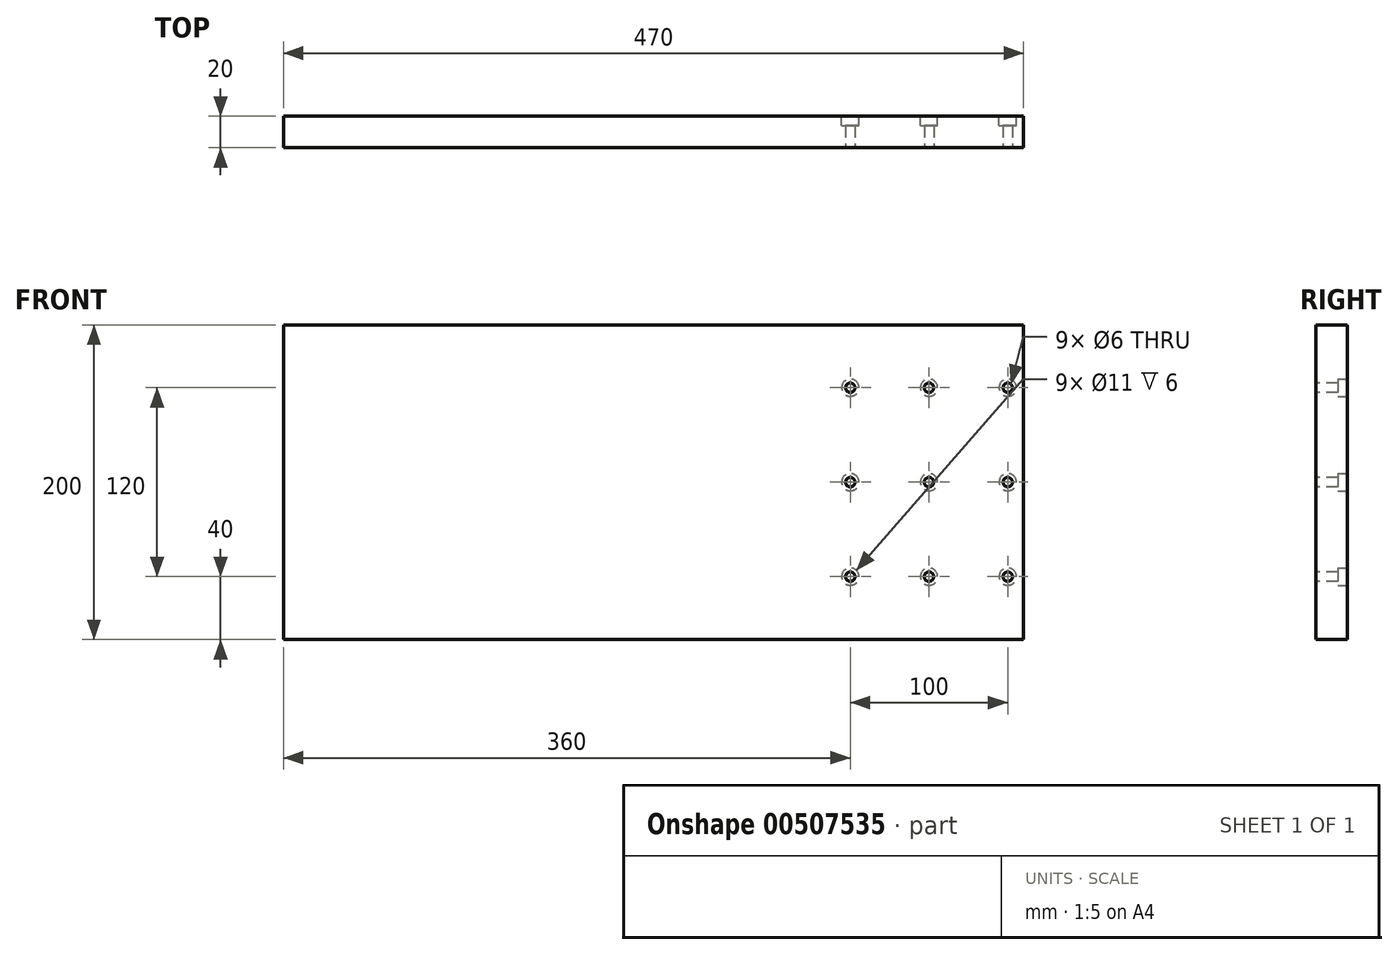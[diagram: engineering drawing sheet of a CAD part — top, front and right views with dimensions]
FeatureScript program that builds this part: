
annotation { "Feature Type Name" : "Feature", "Feature Type Description" : "" }
export const myFeature = defineFeature(function(context is Context, id is Id, definition is map)
    precondition{}
    {
        {
            var Q0;
            Q0=qCreatedBy(makeId("Front.planeOp"),FACE);
            var sketch = newSketch(context, id + "F0", { "sketchPlane" : qUnion([Q0])});
            skLineSegment(sketch, "E0.bottom", {"start": v(0, 0) * mm, "end": v(470, 0) * mm});
            skLineSegment(sketch, "E0.top", {"start": v(0, 200) * mm, "end": v(470, 200) * mm});
            skLineSegment(sketch, "E0.left", {"start": v(0, 0) * mm, "end": v(0, 200) * mm});
            skLineSegment(sketch, "E0.right", {"start": v(470, 0) * mm, "end": v(470, 200) * mm});
            skSolve(sketch);
        }
        {
            var Q0;
            Q0=makeQuery(id+"F0.imprint","IMPRINT",FACE,{"disambiguationData":[TD([[makeQuery(id+"F0.imprint","IMPRINT",EDGE,{"derivedFrom":sQuery(id+"F0.wireOp",EDGE,"E0.bottom")}),1.0]])]});
            extrude(context, id + "F1", {"entities" : qUnion([Q0]), "depth" : 20 * mm});
        }
        {
            var Q0;
            Q0=makeQuery(id+"F1.opExtrude","CAP_FACE",FACE,{"disambiguationData":[OSD([sQuery(id+"F0.wireOp",EDGE,"E0.bottom"),sQuery(id+"F0.wireOp",EDGE,"E0.top"),sQuery(id+"F0.wireOp",EDGE,"E0.left"),sQuery(id+"F0.wireOp",EDGE,"E0.right")])],"isStart":false});
            var sketch = newSketch(context, id + "F2", { "sketchPlane" : qUnion([Q0])});
            skCircle(sketch, "E1", {"center": v(360, 160) * mm, "radius": 3 * mm});
            skCircle(sketch, "E2", {"center": v(360, 100) * mm, "radius": 3 * mm});
            skCircle(sketch, "E3", {"center": v(360, 40) * mm, "radius": 3 * mm});
            skCircle(sketch, "E4", {"center": v(410, 160) * mm, "radius": 3 * mm});
            skCircle(sketch, "E5", {"center": v(410, 100) * mm, "radius": 3 * mm});
            skCircle(sketch, "E6", {"center": v(410, 40) * mm, "radius": 3 * mm});
            skCircle(sketch, "E7", {"center": v(460, 160) * mm, "radius": 3 * mm});
            skCircle(sketch, "E8", {"center": v(460, 100) * mm, "radius": 3 * mm});
            skCircle(sketch, "E9", {"center": v(460, 40) * mm, "radius": 3 * mm});
            skSolve(sketch);
        }
        {
            var Q0;
            Q0 = qSketchRegion(id + "F2", true);
            extrude(context, id + "F3", {"entities" : qUnion([Q0]), "operationType" : NewBodyOperationType.REMOVE, "oppositeDirection" : true, "depth" : 20 * mm, "offsetDistance" : 25 * mm});
        }
        {
            var Q0;
            Q0=makeQuery(id+"F1.opExtrude","CAP_FACE",FACE,{"disambiguationData":[OSD([sQuery(id+"F0.wireOp",EDGE,"E0.bottom"),sQuery(id+"F0.wireOp",EDGE,"E0.top"),sQuery(id+"F0.wireOp",EDGE,"E0.left"),sQuery(id+"F0.wireOp",EDGE,"E0.right")])],"isStart":true});
            var sketch = newSketch(context, id + "F4", { "sketchPlane" : qUnion([Q0])});
            skCircle(sketch, "E10", {"center": v(-460, 160) * mm, "radius": 5.5 * mm});
            skCircle(sketch, "E11", {"center": v(-410, 160) * mm, "radius": 5.5 * mm});
            skCircle(sketch, "E12", {"center": v(-360, 160) * mm, "radius": 5.5 * mm});
            skCircle(sketch, "E13", {"center": v(-360, 100) * mm, "radius": 5.5 * mm});
            skCircle(sketch, "E14", {"center": v(-410, 100) * mm, "radius": 5.5 * mm});
            skCircle(sketch, "E15", {"center": v(-460, 100) * mm, "radius": 5.5 * mm});
            skCircle(sketch, "E16", {"center": v(-460, 40) * mm, "radius": 5.5 * mm});
            skCircle(sketch, "E17", {"center": v(-410, 40) * mm, "radius": 5.5 * mm});
            skCircle(sketch, "E18", {"center": v(-360, 40) * mm, "radius": 5.5 * mm});
            skSolve(sketch);
        }
        {
            var Q0;
            Q0 = qSketchRegion(id + "F4", true);
            extrude(context, id + "F5", {"entities" : qUnion([Q0]), "operationType" : NewBodyOperationType.REMOVE, "oppositeDirection" : true, "depth" : 6 * mm, "offsetDistance" : 25 * mm});
        }
    });
